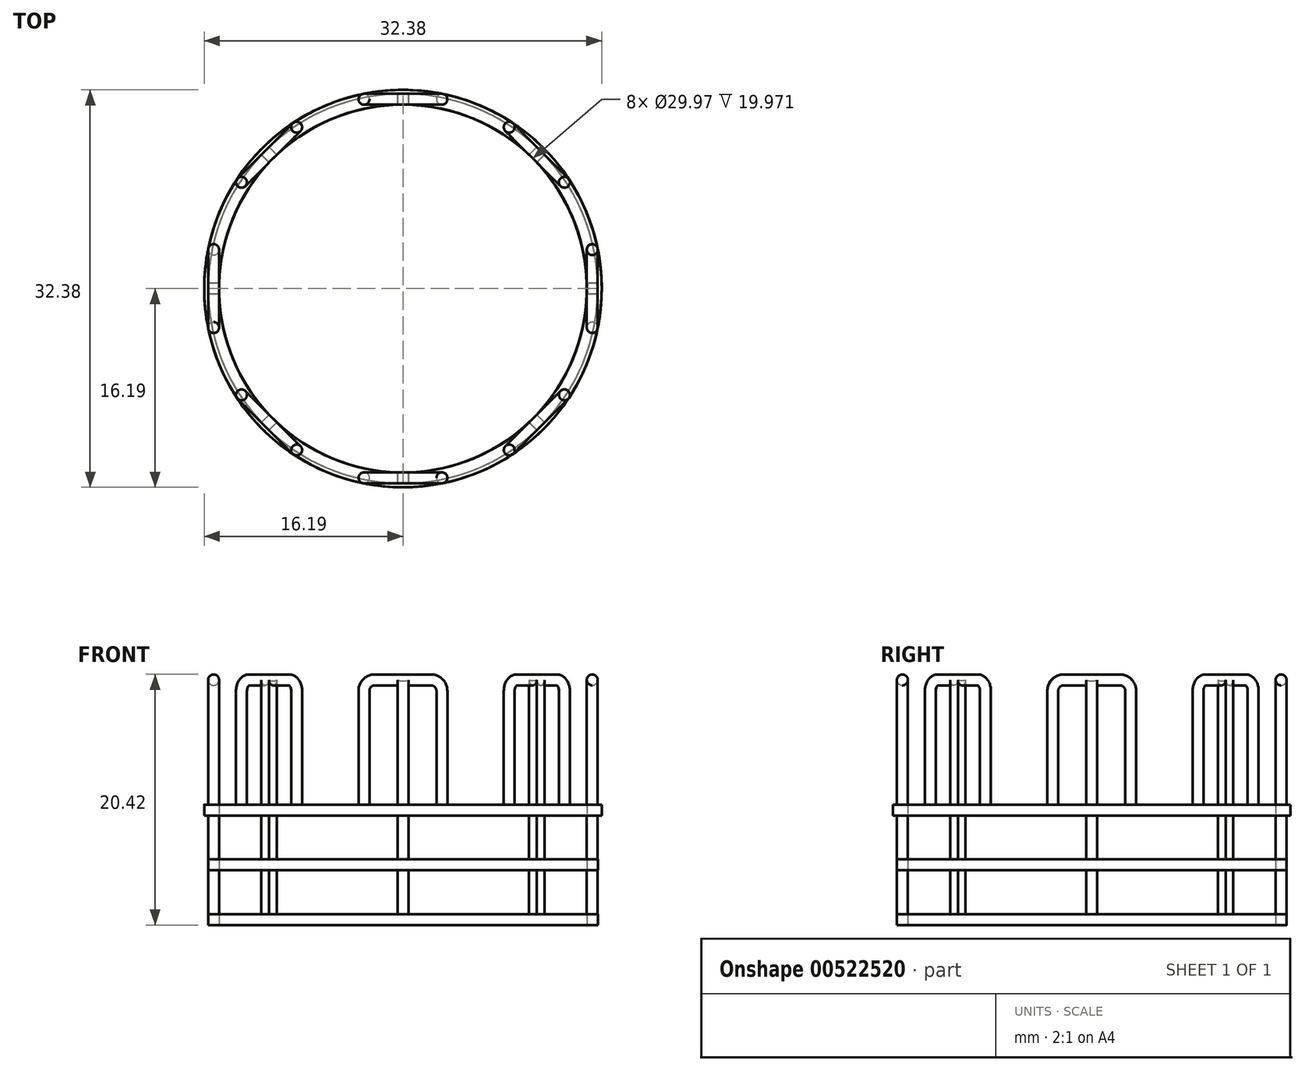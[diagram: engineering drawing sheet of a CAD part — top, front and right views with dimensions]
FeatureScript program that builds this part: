
annotation { "Feature Type Name" : "Feature", "Feature Type Description" : "" }
export const myFeature = defineFeature(function(context is Context, id is Id, definition is map)
    precondition{}
    {
        {
            var Q0;
            Q0=qCreatedBy(makeId("Top.planeOp"),FACE);
            var sketch = newSketch(context, id + "F0", { "sketchPlane" : qUnion([Q0])});
            skCircle(sketch, "E0", {"center": v(0, 0) * mm, "radius": 15.88 * mm});
            skCircle(sketch, "E1.0", {"center": v(0, 0) * mm, "radius": 14.99 * mm});
            skSolve(sketch);
        }
        {
            var Q0;
            Q0=makeQuery(id+"F0.imprint","IMPRINT",FACE,{"disambiguationData":[TD([[makeQuery(id+"F0.imprint","IMPRINT",EDGE,{"derivedFrom":sQuery(id+"F0.wireOp",EDGE,"E0")}),1.0]])]});
            extrude(context, id + "F1", {"entities" : qUnion([Q0]), "depth" : 0.89 * mm, "offsetDistance" : 25.4 * mm});
        }
        {
            var Q0;
            Q0=makeQuery(id+"F1.opExtrude","CAP_FACE",FACE,{"disambiguationData":[OSD([sQuery(id+"F0.wireOp",EDGE,"E0"),sQuery(id+"F0.wireOp",EDGE,"E1.0")])],"isStart":false});
            var sketch = newSketch(context, id + "F2", { "sketchPlane" : qUnion([Q0])});
            skLineSegment(sketch, "E2.bottom", {"start": v(-0.44, -14.98) * mm, "end": v(0.44, -14.98) * mm});
            skLineSegment(sketch, "E2.top", {"start": v(-0.44, -15.87) * mm, "end": v(0.44, -15.87) * mm});
            skLineSegment(sketch, "E2.left", {"start": v(-0.44, -14.98) * mm, "end": v(-0.44, -15.87) * mm});
            skLineSegment(sketch, "E2.right", {"start": v(0.44, -14.98) * mm, "end": v(0.44, -15.87) * mm});
            skPoint(sketch, "E2.middle", {"position": v(0, -15.42) * mm});
            skLineSegment(sketch, "E3.bottom", {"start": v(15.87, 0.44) * mm, "end": v(14.98, 0.44) * mm});
            skLineSegment(sketch, "E3.top", {"start": v(15.87, -0.44) * mm, "end": v(14.98, -0.44) * mm});
            skLineSegment(sketch, "E3.left", {"start": v(15.87, 0.44) * mm, "end": v(15.87, -0.44) * mm});
            skLineSegment(sketch, "E3.right", {"start": v(14.98, 0.44) * mm, "end": v(14.98, -0.44) * mm});
            skPoint(sketch, "E3.middle", {"position": v(15.42, 0) * mm});
            skLineSegment(sketch, "E4.bottom", {"start": v(0.44, 14.98) * mm, "end": v(-0.44, 14.98) * mm});
            skLineSegment(sketch, "E4.top", {"start": v(0.44, 15.87) * mm, "end": v(-0.44, 15.87) * mm});
            skLineSegment(sketch, "E4.left", {"start": v(0.44, 14.98) * mm, "end": v(0.44, 15.87) * mm});
            skLineSegment(sketch, "E4.right", {"start": v(-0.44, 14.98) * mm, "end": v(-0.44, 15.87) * mm});
            skPoint(sketch, "E4.middle", {"position": v(0, 15.42) * mm});
            skLineSegment(sketch, "E5.bottom", {"start": v(-14.98, -0.44) * mm, "end": v(-15.87, -0.44) * mm});
            skLineSegment(sketch, "E5.top", {"start": v(-14.98, 0.44) * mm, "end": v(-15.87, 0.44) * mm});
            skLineSegment(sketch, "E5.left", {"start": v(-14.98, -0.44) * mm, "end": v(-14.98, 0.44) * mm});
            skLineSegment(sketch, "E5.right", {"start": v(-15.87, -0.44) * mm, "end": v(-15.87, 0.44) * mm});
            skPoint(sketch, "E5.middle", {"position": v(-15.42, 0) * mm});
            skSolve(sketch);
        }
        {
            var Q0;
            Q0=makeQuery(id+"F2.imprint","IMPRINT",FACE,{"disambiguationData":[TD([[makeQuery(id+"F2.imprint","IMPRINT",EDGE,{"derivedFrom":sQuery(id+"F2.wireOp",EDGE,"E4.top")}),1.0]])]});
            var Q1;
            {var subQ0=sQuery(id+"F2.wireOp",EDGE,"E5.bottom");Q1=makeQuery(id+"F2.imprint","IMPRINT",FACE,{"disambiguationData":[TD([[makeQuery(id+"F2.imprint","IMPRINT",EDGE,{"derivedFrom":subQ0}),-1.0]])]});}
            var Q2;
            Q2=makeQuery(id+"F2.imprint","IMPRINT",FACE,{"disambiguationData":[TD([[makeQuery(id+"F2.imprint","IMPRINT",EDGE,{"derivedFrom":sQuery(id+"F2.wireOp",EDGE,"E2.top")}),1.0]])]});
            var Q3;
            {var subQ1=sQuery(id+"F2.wireOp",EDGE,"E3.bottom");Q3=makeQuery(id+"F2.imprint","IMPRINT",FACE,{"disambiguationData":[TD([[makeQuery(id+"F2.imprint","IMPRINT",EDGE,{"derivedFrom":subQ1}),1.0]])]});}
            extrude(context, id + "F3", {"entities" : qUnion([Q0, Q1, Q2, Q3]), "operationType" : NewBodyOperationType.ADD, "depth" : 3.57 * mm, "offsetDistance" : 25.4 * mm});
        }
        {
            var Q0;
            Q0=makeQuery(id+"F3.opExtrude","CAP_FACE",FACE,{"disambiguationData":[OSD([sQuery(id+"F0.wireOp",EDGE,"E1.0"),sQuery(id+"F2.wireOp",EDGE,"E4.top"),sQuery(id+"F2.wireOp",EDGE,"E4.left"),sQuery(id+"F2.wireOp",EDGE,"E4.right")])],"isStart":false});
            var sketch = newSketch(context, id + "F4", { "sketchPlane" : qUnion([Q0])});
            skCircle(sketch, "E6", {"center": v(0, 0) * mm, "radius": 15.88 * mm});
            skCircle(sketch, "E7.0", {"center": v(0, 0) * mm, "radius": 14.99 * mm});
            skSolve(sketch);
        }
        {
            var Q0;
            Q0=makeQuery(id+"F4.imprint","IMPRINT",FACE,{"disambiguationData":[TD([[makeQuery(id+"F4.imprint","IMPRINT",EDGE,{"derivedFrom":sQuery(id+"F4.wireOp",EDGE,"E6")}),1.0]])]});
            var Q1;
            Q1=makeQuery(id+"F4.imprint","IMPRINT",FACE,{"disambiguationData":[TD([[makeQuery(id+"F4.imprint","IMPRINT",EDGE,{"derivedFrom":makeQuery(id+"F3.opExtrude","CAP_EDGE",EDGE,{"disambiguationData":[OSD([sQuery(id+"F2.wireOp",EDGE,"E4.top")])],"isStart":false})}),1.0]])]});
            extrude(context, id + "F5", {"entities" : qUnion([Q0, Q1]), "operationType" : NewBodyOperationType.ADD, "depth" : 0.89 * mm, "offsetDistance" : 25.4 * mm});
        }
        {
            var Q0;
            Q0=makeQuery(id+"F5.opExtrude","CAP_FACE",FACE,{"disambiguationData":[OSD([sQuery(id+"F4.wireOp",EDGE,"E6"),sQuery(id+"F4.wireOp",EDGE,"E7.0")])],"isStart":false});
            var sketch = newSketch(context, id + "F6", { "sketchPlane" : qUnion([Q0])});
            skLineSegment(sketch, "E8.bottom", {"start": v(0.44, 14.98) * mm, "end": v(-0.44, 14.98) * mm});
            skLineSegment(sketch, "E8.top", {"start": v(0.44, 15.87) * mm, "end": v(-0.44, 15.87) * mm});
            skLineSegment(sketch, "E8.left", {"start": v(0.44, 14.98) * mm, "end": v(0.44, 15.87) * mm});
            skLineSegment(sketch, "E8.right", {"start": v(-0.44, 14.98) * mm, "end": v(-0.44, 15.87) * mm});
            skPoint(sketch, "E8.middle", {"position": v(0, 15.42) * mm});
            skLineSegment(sketch, "E9.bottom", {"start": v(15.87, -0.44) * mm, "end": v(14.98, -0.44) * mm});
            skLineSegment(sketch, "E9.top", {"start": v(15.87, 0.44) * mm, "end": v(14.98, 0.44) * mm});
            skLineSegment(sketch, "E9.left", {"start": v(15.87, -0.44) * mm, "end": v(15.87, 0.44) * mm});
            skLineSegment(sketch, "E9.right", {"start": v(14.98, -0.44) * mm, "end": v(14.98, 0.44) * mm});
            skPoint(sketch, "E9.middle", {"position": v(15.42, 0) * mm});
            skLineSegment(sketch, "E10.bottom", {"start": v(-0.44, -14.98) * mm, "end": v(0.44, -14.98) * mm});
            skLineSegment(sketch, "E10.top", {"start": v(-0.44, -15.87) * mm, "end": v(0.44, -15.87) * mm});
            skLineSegment(sketch, "E10.left", {"start": v(-0.44, -14.98) * mm, "end": v(-0.44, -15.87) * mm});
            skLineSegment(sketch, "E10.right", {"start": v(0.44, -14.98) * mm, "end": v(0.44, -15.87) * mm});
            skPoint(sketch, "E10.middle", {"position": v(0, -15.42) * mm});
            skLineSegment(sketch, "E11.bottom", {"start": v(-14.98, -0.44) * mm, "end": v(-15.87, -0.44) * mm});
            skLineSegment(sketch, "E11.top", {"start": v(-14.98, 0.44) * mm, "end": v(-15.87, 0.44) * mm});
            skLineSegment(sketch, "E11.left", {"start": v(-14.98, -0.44) * mm, "end": v(-14.98, 0.44) * mm});
            skLineSegment(sketch, "E11.right", {"start": v(-15.87, -0.44) * mm, "end": v(-15.87, 0.44) * mm});
            skPoint(sketch, "E11.middle", {"position": v(-15.42, 0) * mm});
            skSolve(sketch);
        }
        {
            var Q0;
            {var subQ0=sQuery(id+"F6.wireOp",EDGE,"E11.bottom");Q0=makeQuery(id+"F6.imprint","IMPRINT",FACE,{"disambiguationData":[TD([[makeQuery(id+"F6.imprint","IMPRINT",EDGE,{"derivedFrom":subQ0}),-1.0]])]});}
            var Q1;
            Q1=makeQuery(id+"F6.imprint","IMPRINT",FACE,{"disambiguationData":[TD([[makeQuery(id+"F6.imprint","IMPRINT",EDGE,{"derivedFrom":sQuery(id+"F6.wireOp",EDGE,"E8.top")}),1.0]])]});
            var Q2;
            {var subQ1=sQuery(id+"F6.wireOp",EDGE,"E9.bottom");Q2=makeQuery(id+"F6.imprint","IMPRINT",FACE,{"disambiguationData":[TD([[makeQuery(id+"F6.imprint","IMPRINT",EDGE,{"derivedFrom":subQ1}),-1.0]])]});}
            var Q3;
            Q3=makeQuery(id+"F6.imprint","IMPRINT",FACE,{"disambiguationData":[TD([[makeQuery(id+"F6.imprint","IMPRINT",EDGE,{"derivedFrom":sQuery(id+"F6.wireOp",EDGE,"E10.top")}),1.0]])]});
            extrude(context, id + "F7", {"entities" : qUnion([Q0, Q1, Q2, Q3]), "operationType" : NewBodyOperationType.ADD, "depth" : 3.57 * mm, "offsetDistance" : 25.4 * mm});
        }
        {
            var Q0;
            Q0=makeQuery(id+"F7.opExtrude","CAP_FACE",FACE,{"disambiguationData":[OSD([sQuery(id+"F4.wireOp",EDGE,"E7.0"),sQuery(id+"F6.wireOp",EDGE,"E8.top"),sQuery(id+"F6.wireOp",EDGE,"E8.left"),sQuery(id+"F6.wireOp",EDGE,"E8.right")])],"isStart":false});
            var sketch = newSketch(context, id + "F8", { "sketchPlane" : qUnion([Q0])});
            skCircle(sketch, "E12", {"center": v(0, 0) * mm, "radius": 15.88 * mm});
            skCircle(sketch, "E13.0", {"center": v(0, 0) * mm, "radius": 14.99 * mm});
            skSolve(sketch);
        }
        {
            var Q0;
            Q0=makeQuery(id+"F8.imprint","IMPRINT",FACE,{"disambiguationData":[TD([[makeQuery(id+"F8.imprint","IMPRINT",EDGE,{"derivedFrom":sQuery(id+"F8.wireOp",EDGE,"E12")}),1.0]])]});
            var Q1;
            Q1=makeQuery(id+"F8.imprint","IMPRINT",FACE,{"disambiguationData":[TD([[makeQuery(id+"F8.imprint","IMPRINT",EDGE,{"derivedFrom":makeQuery(id+"F7.opExtrude","CAP_EDGE",EDGE,{"disambiguationData":[OSD([sQuery(id+"F6.wireOp",EDGE,"E8.top")])],"isStart":false})}),1.0]])]});
            extrude(context, id + "F9", {"entities" : qUnion([Q0, Q1]), "operationType" : NewBodyOperationType.ADD, "depth" : 0.89 * mm, "offsetDistance" : 25.4 * mm});
        }
        {
            var Q0;
            Q0=makeQuery(id+"F9.opExtrude","CAP_FACE",FACE,{"disambiguationData":[OSD([sQuery(id+"F8.wireOp",EDGE,"E12"),sQuery(id+"F8.wireOp",EDGE,"E13.0")])],"isStart":false});
            var sketch = newSketch(context, id + "F10", { "sketchPlane" : qUnion([Q0])});
            skLineSegment(sketch, "E14.bottom", {"start": v(0.44, -15.87) * mm, "end": v(-0.44, -15.87) * mm});
            skLineSegment(sketch, "E14.top", {"start": v(0.44, -14.98) * mm, "end": v(-0.44, -14.98) * mm});
            skLineSegment(sketch, "E14.left", {"start": v(0.44, -15.87) * mm, "end": v(0.44, -14.98) * mm});
            skLineSegment(sketch, "E14.right", {"start": v(-0.44, -15.87) * mm, "end": v(-0.44, -14.98) * mm});
            skPoint(sketch, "E14.middle", {"position": v(0, -15.42) * mm});
            skPoint(sketch, "E15", {"position": v(-3.18, -15.1) * mm});
            skPoint(sketch, "E16", {"position": v(0.44, -15.42) * mm});
            skCircle(sketch, "E17", {"center": v(-3.17, -15.42) * mm, "radius": 0.44 * mm});
            skCircle(sketch, "E18", {"center": v(3.18, -15.42) * mm, "radius": 0.44 * mm});
            skSolve(sketch);
        }
        {
            var Q0;
            {var subQ0=sQuery(id+"F10.wireOp",EDGE,"E17");var subQ1=makeQuery(id+"F10.imprint","INTERSECT",VERTEX,{"derivedFrom":[makeQuery(id+"F9.opExtrude","CAP_EDGE",EDGE,{"disambiguationData":[OSD([sQuery(id+"F8.wireOp",EDGE,"E12")])],"isStart":false}),subQ0]});Q0=makeQuery(id+"F10.imprint","IMPRINT",FACE,{"disambiguationData":[TD([[makeQuery(id+"F10.imprint","IMPRINT",EDGE,{"disambiguationData":[TD([[subQ1,1.0]])],"derivedFrom":subQ0}),1.0]])]});}
            var Q1;
            Q1=makeQuery(id+"F10.imprint","IMPRINT",FACE,{"disambiguationData":[TD([[makeQuery(id+"F10.imprint","IMPRINT",EDGE,{"derivedFrom":sQuery(id+"F10.wireOp",EDGE,"E14.bottom")}),-1.0]])]});
            var Q2;
            {var subQ0=sQuery(id+"F10.wireOp",EDGE,"E18");var subQ1=makeQuery(id+"F10.imprint","INTERSECT",VERTEX,{"derivedFrom":[makeQuery(id+"F9.opExtrude","CAP_EDGE",EDGE,{"disambiguationData":[OSD([sQuery(id+"F8.wireOp",EDGE,"E12")])],"isStart":false}),subQ0]});Q2=makeQuery(id+"F10.imprint","IMPRINT",FACE,{"disambiguationData":[TD([[makeQuery(id+"F10.imprint","IMPRINT",EDGE,{"disambiguationData":[TD([[subQ1,1.0]])],"derivedFrom":subQ0}),1.0]])]});}
            extrude(context, id + "F11", {"entities" : qUnion([Q0, Q1, Q2]), "operationType" : NewBodyOperationType.ADD, "depth" : 7.62 * mm, "offsetDistance" : 25.4 * mm});
        }
        {
            var Q0;
            Q0=makeQuery(id+"F11.opExtrude","CAP_FACE",FACE,{"disambiguationData":[OSD([sQuery(id+"F10.wireOp",EDGE,"E17")])],"isStart":false});
            var sketch = newSketch(context, id + "F12", { "sketchPlane" : qUnion([Q0])});
            skPoint(sketch, "E19", {"position": v(-3.17, -15.42) * mm});
            skPoint(sketch, "E20", {"position": v(3.98, -15.42) * mm});
            skSolve(sketch);
        }
        {
            var Q0;
            Q0=makeQuery(id+"F11.opExtrude","SWEPT_FACE",FACE,{"disambiguationData":[OSD([sQuery(id+"F10.wireOp",EDGE,"E14.bottom")])]});
            cPlane(context, id + "F13", {"entities" : qUnion([Q0]), "cplaneType" : CPlaneType.OFFSET, "offset" : 0.44 * mm, "oppositeDirection" : true, "width" : 152.4 * mm, "height" : 152.4 * mm});
        }
        {
            var Q0;
            Q0=qCreatedBy(id+"F13.planeOp",FACE);
            var sketch = newSketch(context, id + "F14", { "sketchPlane" : qUnion([Q0])});
            skLineSegment(sketch, "E21", {"start": v(-3.18, 17.43) * mm, "end": v(-3.18, 19.08) * mm});
            skLineSegment(sketch, "E22", {"start": v(-2.29, 19.97) * mm, "end": v(2.29, 19.97) * mm});
            skLineSegment(sketch, "E23", {"start": v(3.17, 17.43) * mm, "end": v(3.17, 19.08) * mm});
            skPoint(sketch, "E24.orphan", {"position": v(-3.62, 17.43) * mm});
            skPoint(sketch, "E25.0.end.orphan", {"position": v(-2.73, 17.43) * mm});
            skPoint(sketch, "E26.orphan", {"position": v(2.73, 17.43) * mm});
            skPoint(sketch, "E27.0.end.orphan", {"position": v(3.62, 17.43) * mm});
            skPoint(sketch, "E28.visualSharp", {"position": v(-3.18, 19.97) * mm});
            skArc(sketch, "E28.filletArc", {"start": v(-2.29, 19.97) * mm, "mid": v(-2.91, 19.71) * mm, "end": v(-3.18, 19.08) * mm});
            skPoint(sketch, "E29.visualSharp", {"position": v(3.17, 19.97) * mm});
            skArc(sketch, "E29.filletArc", {"start": v(3.17, 19.08) * mm, "mid": v(2.91, 19.71) * mm, "end": v(2.29, 19.97) * mm});
            skSolve(sketch);
        }
        {
            var Q0;
            Q0=makeQuery(id+"F12.imprint","IMPRINT",FACE,{"disambiguationData":[TD([[makeQuery(id+"F12.imprint","IMPRINT",EDGE,{"derivedFrom":makeQuery(id+"F11.opExtrude","CAP_EDGE",EDGE,{"disambiguationData":[OSD([sQuery(id+"F10.wireOp",EDGE,"E17")])],"isStart":false})}),1.0]])]});
            var Q1;
            Q1 = qConstructionFilter(qBodyType(qCreatedBy(id + "F14" ,EDGE), BodyType.WIRE), ConstructionObject.NO);
            sweep(context, id + "F15", {"operationType" : NewBodyOperationType.ADD, "profiles" : qUnion([Q0]), "path" : qUnion([Q1])});
        }
        {
            var Q0;
            Q0=makeQuery(id+"F9.opExtrude","CAP_FACE",FACE,{"disambiguationData":[OSD([sQuery(id+"F8.wireOp",EDGE,"E12"),sQuery(id+"F8.wireOp",EDGE,"E13.0")])],"isStart":false});
            var sketch = newSketch(context, id + "F16", { "sketchPlane" : qUnion([Q0])});
            skCircle(sketch, "E30", {"center": v(0, 0) * mm, "radius": 16.2 * mm});
            skCircle(sketch, "E31", {"center": v(0, 0) * mm, "radius": 14.99 * mm});
            skSolve(sketch);
        }
        {
            var Q0;
            Q0 = qSketchRegion(id + "F16", true);
            extrude(context, id + "F17", {"entities" : qUnion([Q0]), "operationType" : NewBodyOperationType.ADD, "oppositeDirection" : true, "depth" : 0.89 * mm, "offsetDistance" : 25.4 * mm});
        }
        {
            var Q0;
            Q0=makeQuery(id+"F11.opExtrude","CAP_FACE",FACE,{"disambiguationData":[OSD([sQuery(id+"F8.wireOp",EDGE,"E13.0"),sQuery(id+"F10.wireOp",EDGE,"E14.bottom"),sQuery(id+"F10.wireOp",EDGE,"E14.top"),sQuery(id+"F10.wireOp",EDGE,"E14.left"),sQuery(id+"F10.wireOp",EDGE,"E14.right")])],"isStart":false});
            extrude(context, id + "F18", {"entities" : qUnion([Q0]), "operationType" : NewBodyOperationType.ADD, "depth" : 2.54 * mm, "offsetDistance" : 25.4 * mm});
        }
        {
            var Q0;
            Q0=makeQuery(id+"F1.opExtrude","SWEPT_BODY",BODY,{"disambiguationData":[OSD([sQuery(id+"F0.wireOp",EDGE,"E0"),sQuery(id+"F0.wireOp",EDGE,"E1.0")])]});
            var Q1;
            Q1=makeQuery(id+"F1.opExtrude","CAP_EDGE",EDGE,{"disambiguationData":[OSD([sQuery(id+"F0.wireOp",EDGE,"E1.0")])],"isStart":true});
            circularPattern(context, id + "F19", {"entities" : qUnion([Q0]), "axis" : qUnion([Q1]), "angle" : 360 * degree, "instanceCount" : 8, "equalSpace" : true});
        }
    });
